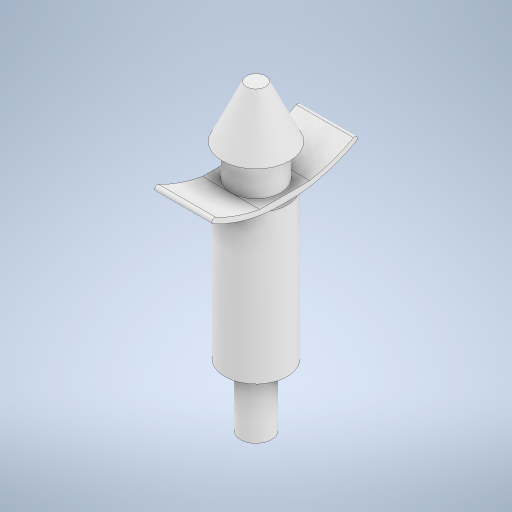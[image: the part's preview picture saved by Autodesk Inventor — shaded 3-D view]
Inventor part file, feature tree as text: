
AUTODESK INVENTOR PART (.ipt)
format: ipt  version: 2024.2 (Build 282272000, 272)  size: 302,592 bytes
history: native  units: mm
features: sketch x1, revolve x1, extrude x1, mirror x1
ambient origin geometry x8: Origin, YZ Plane, XZ Plane, XY Plane, X Axis, Y Axis, Z Axis, Center Point
bodies: Solid1 (feature_tree)
feature tree (4):
  sketch  "Sketch1"  dims[d0=3.0mm d1=6.0mm d3=6.0mm d4=5.0mm d5=6.5mm d9=8.8mm d10=4.363323mm d11=4.8mm d12=90.0deg d13=5.5mm d14=0.0mm d15=15.0mm d17=14.0mm d18=0.5mm d19=1.6mm]
  revolve  "Revolution1"  [1 undecoded]
  extrude  "Extrusion1"  Depth=14.0mm
  mirror  "Mirror1"
note: 1 required parameter value undecoded (feature->parameter linkage not recoverable at this tier; creation-order binding heuristic only, values carry confidence <= 0.55)
